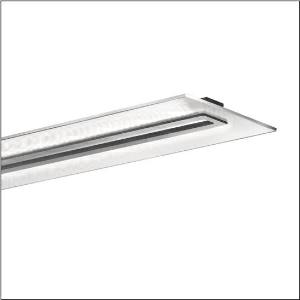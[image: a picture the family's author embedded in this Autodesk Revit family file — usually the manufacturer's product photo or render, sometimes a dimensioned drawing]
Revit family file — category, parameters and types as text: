
# Revit family: vega_r__11_5mn238dle0s_e1af
name_source: partatom
category: Lighting Fixtures
units: mm (PartAtom-declared; Revit-internal decimal feet)

## family parameters
Cut with Voids When Loaded = No
Host = Face
Light Source = No
Part Type = Normal
Room Calculation Point = No
Round Connector Dimension = Use Diameter
Shared = No

## types (1)
- --- (1 x LED 4000K / CRI = 80 (unbekannt), 8130 lm, 4000K)
    Apparent Load = 62 VA
    CIE Flux Codes = 61 86 97 62 100
    Color Rendering = 80
    Color Temperature = 4000K
    Default Elevation = 1800 mm
    Description = Vega® 11, office luminaire, primary light control with prismatic reflector, of PMMA, transparent prismatic structure, CAT 2 (L<= 1500cd/m²), light emission: direct/indirect distribution, primary light characteristic: symmetric, installation type: suspended mounting, surface-mounted, LED, rated luminous flux: 8.130lm, luminous efficacy: 131lm/W, light colour: 840, colour temperature: 4000K, control gear: ECG, with terminal, 3+2-pole, max. 2.5mm², mains connection: 230V, AC, 50Hz, connection cable inclusive, cable length: 1,5m, rated input power: 62W, luminaire housing, rectangular, rounded, of aluminium section, anodised, metallic grey (RAL 9006), length: 1.250mm, width: 350mm, height: 43mm, luminaire housing, lower part, of aluminium section, anodised, metallic grey (RAL 9006), of PC, grey, protection rating (complete): IP20, insulation class (complete): insulation class I (protective earthing), certification: CE, permissible operating ambient temperature: 0..+35°C, standard: EN 50419, packaging unit: 1 piece
    Height = 40 mm  [stored 0.131234 ft]
    Lamp = 1 x LED 4000K / CRI >= 80 (unbekannt)
    Lamp Light Flux = 8130 lm
    Lamp count = 1
    Length = 1250 mm
    Luminous efficacy = 131 lm/W
    Manufacturer = Siteco
    ModVariant = No
    Model = 5MN238DLE0S
    Mounting Place = Ceiling
    Mounting Type = Pendant
    Number of Poles = 1
    OnlyDefault = Yes
    Power Factor = 1
    Product Name = Vega® 11
    Product group = office luminaire | ceiling pendant
    ProductGroupID = 902
    Protection Class = Protection class I
    Protection Degree = IP 20
    RLX_Detail_Level = 1
    RLX_Emergency_Light_Flux = 0 lm
    RLX_Emergency_Type = 0
    RLX_Emergency_Type_DB = No
    RlxData = <blob elided: 63129 chars, md5=cbe918fd>
    Socket = socket
    Standby Power = 0 W
    System Light Flux = 8130 lm
    System Power = 62 W
    Type Comments = factory setting: luminous flux: 100 % | dim-lin: 254 | 458 mA
    Type Image = l_1004807.jpg
    URL = http://relux.com
    VarID = @adj_149877
    Voltage = 0 V
    Weight = 0.00 kg
    Width = 350 mm

note: [stored X ft] marks values corroborated as IEEE doubles in the binary element streams (Revit-internal decimal feet)

## geometry (parser evidence)
native form markers: Blend x4, Sweep x12
no freeform markers — native parametric forms only
